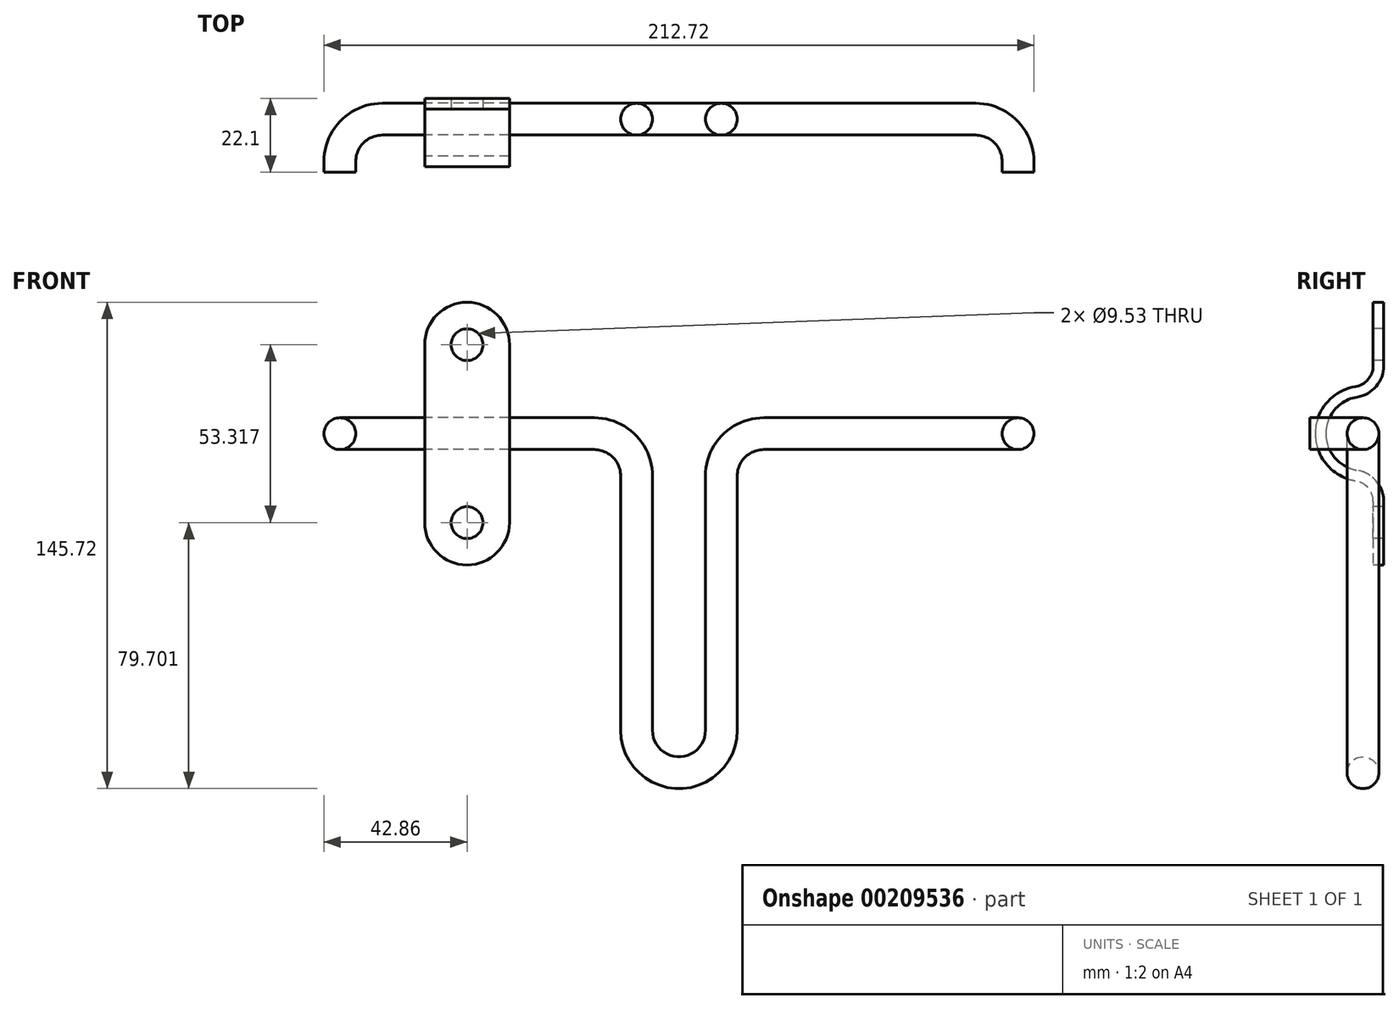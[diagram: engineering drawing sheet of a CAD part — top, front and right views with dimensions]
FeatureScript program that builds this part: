
annotation { "Feature Type Name" : "Feature", "Feature Type Description" : "" }
export const myFeature = defineFeature(function(context is Context, id is Id, definition is map)
    precondition{}
    {
        {
            var Q0;
            Q0=qCreatedBy(makeId("Front.planeOp"),FACE);
            var sketch = newSketch(context, id + "F0", { "sketchPlane" : qUnion([Q0])});
            skLineSegment(sketch, "E0", {"start": v(-88.9, 88.9) * mm, "end": v(-25.4, 88.9) * mm});
            skLineSegment(sketch, "E1", {"start": v(-12.7, 76.2) * mm, "end": v(-12.7, 0) * mm});
            skLineSegment(sketch, "E2", {"start": v(12.7, 0) * mm, "end": v(12.7, 76.2) * mm});
            skLineSegment(sketch, "E3", {"start": v(25.4, 88.9) * mm, "end": v(88.9, 88.9) * mm});
            skArc(sketch, "E4", {"start": v(-12.7, 0) * mm, "mid": v(0, -12.7) * mm, "end": v(12.7, 0) * mm});
            skPoint(sketch, "E5.visualSharp", {"position": v(-12.7, 88.9) * mm});
            skArc(sketch, "E5.filletArc", {"start": v(-12.7, 76.2) * mm, "mid": v(-16.42, 85.18) * mm, "end": v(-25.4, 88.9) * mm});
            skPoint(sketch, "E6.visualSharp", {"position": v(12.7, 88.9) * mm});
            skArc(sketch, "E6.filletArc", {"start": v(25.4, 88.9) * mm, "mid": v(16.42, 85.18) * mm, "end": v(12.7, 76.2) * mm});
            skSolve(sketch);
        }
        {
            var Q0;
            Q0=sQuery(id+"F0.wireOp",EDGE,"E3");
            var Q1;
            Q1=sQuery(id+"F0.wireOp",VERTEX,"E3.end");
            cPlane(context, id + "F1", {"entities" : qUnion([Q0, Q1]), "cplaneType" : CPlaneType.CURVE_POINT, "offset" : 152.4 * mm, "width" : 152.4 * mm, "height" : 152.4 * mm});
        }
        {
            var Q0;
            Q0=qCreatedBy(id+"F1.planeOp",FACE);
            var sketch = newSketch(context, id + "F2", { "sketchPlane" : qUnion([Q0])});
            skCircle(sketch, "E7", {"center": v(0, 88.9) * mm, "radius": 4.76 * mm});
            skSolve(sketch);
        }
        {
            var Q0;
            Q0=makeQuery(id+"F2.imprint","IMPRINT",FACE,{"disambiguationData":[TD([[makeQuery(id+"F2.imprint","IMPRINT",EDGE,{"derivedFrom":sQuery(id+"F2.wireOp",EDGE,"E7")}),1.0]])]});
            var Q1;
            Q1=sQuery(id+"F0.wireOp",EDGE,"E3");
            var Q2;
            Q2=sQuery(id+"F0.wireOp",EDGE,"E6.filletArc");
            var Q3;
            Q3=sQuery(id+"F0.wireOp",EDGE,"E2");
            var Q4;
            Q4=sQuery(id+"F0.wireOp",EDGE,"E4");
            var Q5;
            Q5=sQuery(id+"F0.wireOp",EDGE,"E1");
            var Q6;
            Q6=sQuery(id+"F0.wireOp",EDGE,"E5.filletArc");
            var Q7;
            Q7=sQuery(id+"F0.wireOp",EDGE,"E0");
            sweep(context, id + "F3", {"profiles" : qUnion([Q0]), "path" : qUnion([Q1, Q2, Q3, Q4, Q5, Q6, Q7])});
        }
        {
            var Q0;
            Q0=qCreatedBy(id+"F1.planeOp",FACE);
            var sketch = newSketch(context, id + "F4", { "sketchPlane" : qUnion([Q0])});
            skLineSegment(sketch, "E8", {"start": v(-12.7, 123.03) * mm, "end": v(-12.7, 103.18) * mm});
            skSolve(sketch);
        }
        {
            var Q0;
            Q0=makeQuery(id+"F4.imprint","IMPRINT",FACE,{"disambiguationData":[TD([[sQuery(id+"F4.imprint",EDGE,"58b7934a-6e32-410e-af57-045cd2e2f83f.0.0"),1.0]])]});
            var Q1;
            Q1=makeQuery(id+"F2.imprint","IMPRINT",FACE,{"disambiguationData":[TD([[makeQuery(id+"F2.imprint","IMPRINT",EDGE,{"derivedFrom":sQuery(id+"F2.wireOp",EDGE,"E7")}),1.0]])]});
            var Q2;
            Q2=sQuery(id+"F4.wireOp",EDGE,"E8");
            revolve(context, id + "F5", {"entities" : qUnion([Q0, Q1]), "axis" : qUnion([Q2]), "revolveType" : RevolveType.ONE_DIRECTION, "angle" : 90 * degree});
        }
        {
            var Q0;
            Q0=makeQuery(id+"F5.opRevolve","CAP_FACE",FACE,{"disambiguationData":[OSD([makeQuery(id+"F4.imprint","IMPRINT",FACE,{"disambiguationData":[TD([[sQuery(id+"F4.imprint",EDGE,"58b7934a-6e32-410e-af57-045cd2e2f83f.0.0"),1.0]])]})])],"isStart":false});
            var Q1;
            Q1=makeQuery(id+"F5.opRevolve","CAP_FACE",FACE,{"disambiguationData":[OSD([sQuery(id+"F2.wireOp",EDGE,"E7")])],"isStart":false});
            extrude(context, id + "F6", {"entities" : qUnion([Q0, Q1]), "operationType" : NewBodyOperationType.ADD, "depth" : 3.17 * mm});
        }
        {
            var Q0;
            Q0=makeQuery(id+"F5.opRevolve","SWEPT_BODY",BODY,{"disambiguationData":[OSD([sQuery(id+"F2.wireOp",EDGE,"E7")])]});
            var Q1;
            Q1=qCreatedBy(makeId("Right.planeOp"),FACE);
            mirror(context, id + "F7", {"entities" : qUnion([Q0]), "mirrorPlane" : qUnion([Q1])});
        }
        {
            var Q0;
            Q0=makeQuery(id+"F7.opPattern","COPY",BODY,{"derivedFrom":makeQuery(id+"F5.opRevolve","SWEPT_BODY",BODY,{"disambiguationData":[OSD([sQuery(id+"F2.wireOp",EDGE,"E7")])]}),"instanceName":"1"});
            var Q1;
            Q1=makeQuery(id+"F3.opSweep","SWEPT_BODY",BODY,{"disambiguationData":[OSD([sQuery(id+"F0.wireOp",EDGE,"E0"),sQuery(id+"F2.wireOp",EDGE,"E7")])]});
            var Q2;
            Q2=makeQuery(id+"F5.opRevolve","SWEPT_BODY",BODY,{"disambiguationData":[OSD([sQuery(id+"F2.wireOp",EDGE,"E7")])]});
            booleanBodies(context, id + "F8", {"operationType" : BooleanOperationType.UNION, "tools" : qUnion([Q0, Q1, Q2])});
        }
        {
            var Q0;
            Q0=qCreatedBy(makeId("Right.planeOp"),FACE);
            cPlane(context, id + "F9", {"entities" : qUnion([Q0]), "cplaneType" : CPlaneType.OFFSET, "offset" : 76.2 * mm, "oppositeDirection" : true, "width" : 152.4 * mm, "height" : 152.4 * mm});
        }
        {
            var Q0;
            Q0=qCreatedBy(id+"F9.planeOp",FACE);
            var sketch = newSketch(context, id + "F10", { "sketchPlane" : qUnion([Q0])});
            skLineSegment(sketch, "E9", {"start": v(4.76, 144.02) * mm, "end": v(4.76, 64.46) * mm, "construction": true});
            skCircle(sketch, "E10.0", {"center": v(0, 88.9) * mm, "radius": 4.76 * mm, "construction": true});
            skArc(sketch, "E11", {"start": v(-2.29, 103) * mm, "mid": v(-14.29, 88.9) * mm, "end": v(-2.29, 74.8) * mm});
            skLineSegment(sketch, "E12", {"start": v(3.05, 109.27) * mm, "end": v(3.05, 128.26) * mm});
            skLineSegment(sketch, "E13", {"start": v(3.05, 68.53) * mm, "end": v(3.05, 49.54) * mm});
            skPoint(sketch, "E14.visualSharp", {"position": v(3.05, 102.86) * mm});
            skArc(sketch, "E14.filletArc", {"start": v(-2.29, 103) * mm, "mid": v(1.53, 105.16) * mm, "end": v(3.05, 109.27) * mm});
            skPoint(sketch, "E15.visualSharp", {"position": v(3.05, 74.94) * mm});
            skArc(sketch, "E15.filletArc", {"start": v(3.05, 68.53) * mm, "mid": v(1.53, 72.64) * mm, "end": v(-2.29, 74.8) * mm});
            skLineSegment(sketch, "E16.0", {"start": v(6.22, 109.27) * mm, "end": v(6.22, 128.26) * mm});
            skArc(sketch, "E16.1", {"start": v(-1.78, 99.87) * mm, "mid": v(3.95, 103.1) * mm, "end": v(6.22, 109.27) * mm});
            skArc(sketch, "E16.2", {"start": v(-1.78, 99.87) * mm, "mid": v(-11.11, 88.9) * mm, "end": v(-1.78, 77.93) * mm});
            skArc(sketch, "E16.3", {"start": v(6.22, 68.53) * mm, "mid": v(3.95, 74.7) * mm, "end": v(-1.78, 77.93) * mm});
            skLineSegment(sketch, "E16.4", {"start": v(6.22, 68.53) * mm, "end": v(6.22, 49.54) * mm});
            skLineSegment(sketch, "E17", {"start": v(6.22, 128.26) * mm, "end": v(3.05, 128.26) * mm});
            skLineSegment(sketch, "E18", {"start": v(6.22, 49.54) * mm, "end": v(3.05, 49.54) * mm});
            skSolve(sketch);
        }
        {
            var Q0;
            Q0=makeQuery(id+"F10.imprint","IMPRINT",FACE,{"disambiguationData":[TD([[makeQuery(id+"F10.imprint","IMPRINT",EDGE,{"derivedFrom":sQuery(id+"F10.wireOp",EDGE,"E11")}),1.0]])]});
            extrude(context, id + "F11", {"entities" : qUnion([Q0]), "depth" : 25.4 * mm});
        }
        {
            var Q0;
            Q0=makeQuery(id+"F11.opExtrude","CAP_EDGE",EDGE,{"disambiguationData":[OSD([sQuery(id+"F10.wireOp",EDGE,"E17")])],"isStart":true});
            var Q1;
            Q1=makeQuery(id+"F11.opExtrude","CAP_EDGE",EDGE,{"disambiguationData":[OSD([sQuery(id+"F10.wireOp",EDGE,"E17")])],"isStart":false});
            var Q2;
            Q2=makeQuery(id+"F11.opExtrude","CAP_EDGE",EDGE,{"disambiguationData":[OSD([sQuery(id+"F10.wireOp",EDGE,"E18")])],"isStart":false});
            var Q3;
            Q3=makeQuery(id+"F11.opExtrude","CAP_EDGE",EDGE,{"disambiguationData":[OSD([sQuery(id+"F10.wireOp",EDGE,"E18")])],"isStart":true});
            fillet(context, id + "F12", {"entities" : qUnion([Q0, Q1, Q2, Q3]), "radius" : 12.7 * mm, "tangentPropagation" : true, "allowEdgeOverflow" : false});
        }
        {
            var Q0;
            Q0=makeQuery(id+"F11.opExtrude","SWEPT_FACE",FACE,{"disambiguationData":[OSD([sQuery(id+"F10.wireOp",EDGE,"E12")])]});
            var sketch = newSketch(context, id + "F13", { "sketchPlane" : qUnion([Q0])});
            skCircle(sketch, "E19", {"center": v(-63.5, 115.56) * mm, "radius": 4.76 * mm});
            skCircle(sketch, "E20", {"center": v(-63.5, 62.24) * mm, "radius": 4.76 * mm});
            skSolve(sketch);
        }
        {
            var Q0;
            Q0=makeQuery(id+"F13.imprint","IMPRINT",FACE,{"disambiguationData":[TD([[makeQuery(id+"F13.imprint","IMPRINT",EDGE,{"derivedFrom":sQuery(id+"F13.wireOp",EDGE,"E19")}),1.0]])]});
            var Q1;
            Q1=makeQuery(id+"F13.imprint","IMPRINT",FACE,{"disambiguationData":[TD([[makeQuery(id+"F13.imprint","IMPRINT",EDGE,{"derivedFrom":sQuery(id+"F13.wireOp",EDGE,"E20")}),1.0]])]});
            extrude(context, id + "F14", {"entities" : qUnion([Q0, Q1]), "operationType" : NewBodyOperationType.REMOVE, "endBound" : BoundingType.THROUGH_ALL, "oppositeDirection" : true, "depth" : 25.4 * mm});
        }
        {
            var Q0;
            Q0=qCreatedBy(makeId("Front.planeOp"),FACE);
            cPlane(context, id + "F15", {"entities" : qUnion([Q0]), "cplaneType" : CPlaneType.OFFSET, "offset" : 4.76 * mm, "oppositeDirection" : true, "width" : 152.4 * mm, "height" : 152.4 * mm});
        }
    });
